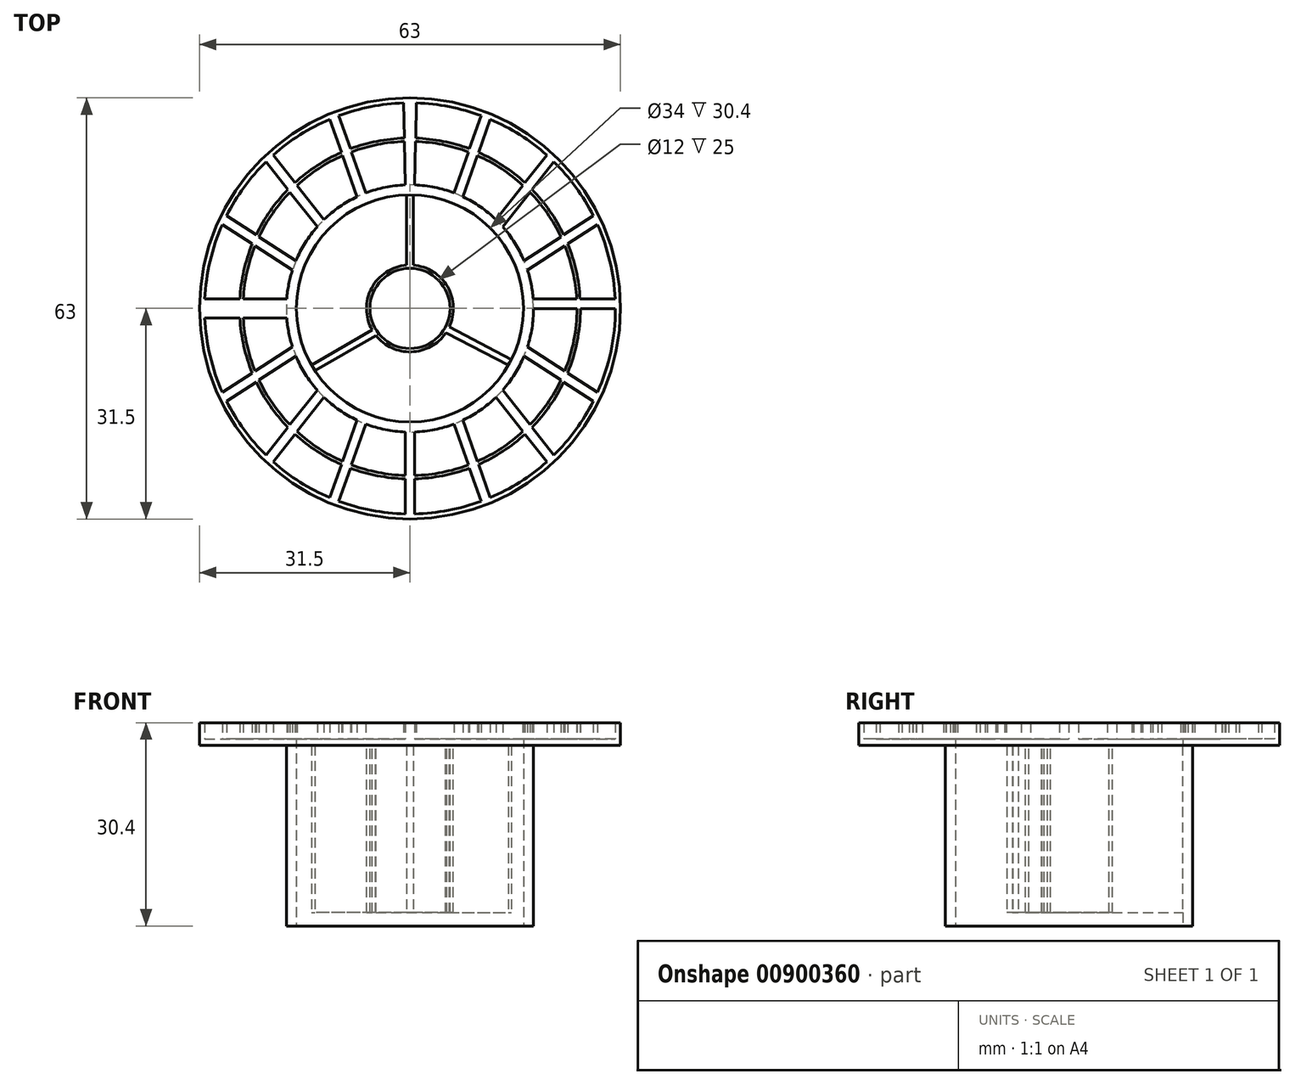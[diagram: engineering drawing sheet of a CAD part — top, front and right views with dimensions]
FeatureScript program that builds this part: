
annotation { "Feature Type Name" : "Feature", "Feature Type Description" : "" }
export const myFeature = defineFeature(function(context is Context, id is Id, definition is map)
    precondition{}
    {
        {
            var Q0;
            Q0=qCreatedBy(makeId("Top.planeOp"),FACE);
            var sketch = newSketch(context, id + "F0", { "sketchPlane" : qUnion([Q0])});
            skCircle(sketch, "E0", {"center": v(0, 0) * mm, "radius": 31.5 * mm});
            skArc(sketch, "E1", {"start": v(-0.7, 18.49) * mm, "mid": v(-3.7, 18.13) * mm, "end": v(-6.6, 17.29) * mm});
            skCircle(sketch, "E2", {"center": v(0, 0) * mm, "radius": 17 * mm});
            skArc(sketch, "E3", {"start": v(-0.85, 25.49) * mm, "mid": v(-4.94, 25.02) * mm, "end": v(-8.9, 23.9) * mm});
            skArc(sketch, "E4", {"start": v(-0.84, 24.99) * mm, "mid": v(-4.85, 24.52) * mm, "end": v(-8.74, 23.42) * mm});
            skArc(sketch, "E5", {"start": v(-0.96, 30.74) * mm, "mid": v(-5.88, 30.18) * mm, "end": v(-10.64, 28.85) * mm});
            skLineSegment(sketch, "E6.MirrorCS", {"start": v(0.96, 30.74) * mm, "end": v(0.85, 25.49) * mm});
            skPoint(sketch, "E7.start.orphan", {"position": v(0, 31.5) * mm});
            skLineSegment(sketch, "E8.trimOffspring", {"start": v(0.84, 24.99) * mm, "end": v(0.71, 18.49) * mm});
            skLineSegment(sketch, "E9", {"start": v(0.71, -18.49) * mm, "end": v(0.71, -24.99) * mm});
            skLineSegment(sketch, "E10", {"start": v(18.5, -0.03) * mm, "end": v(25, -0.03) * mm});
            skPoint(sketch, "E11.start.orphan", {"position": v(17, 0) * mm});
            skArc(sketch, "E12.trimOffspring", {"start": v(25.46, 1.42) * mm, "mid": v(24.87, 5.61) * mm, "end": v(23.6, 9.66) * mm});
            skArc(sketch, "E13.trimOffspring", {"start": v(24.96, 1.42) * mm, "mid": v(24.4, 5.47) * mm, "end": v(23.17, 9.38) * mm});
            skArc(sketch, "E14.trimOffspring", {"start": v(30.72, 1.42) * mm, "mid": v(29.92, 7.1) * mm, "end": v(28.07, 12.55) * mm});
            skLineSegment(sketch, "E15.trimOffspring", {"start": v(25.5, -0.03) * mm, "end": v(30.75, -0.03) * mm});
            skArc(sketch, "E16.trimOffspring", {"start": v(18.5, -0.14) * mm, "mid": v(18.5, -0.09) * mm, "end": v(18.5, -0.03) * mm});
            skPoint(sketch, "E17.orphan", {"position": v(0.71, -16.99) * mm});
            skPoint(sketch, "E18.orphan", {"position": v(-0.7, -16.99) * mm});
            skArc(sketch, "E19.trimOffspring", {"start": v(0.71, -24.99) * mm, "mid": v(4.8, -24.54) * mm, "end": v(8.74, -23.42) * mm});
            skArc(sketch, "E20.trimOffspring", {"start": v(0.71, -25.5) * mm, "mid": v(4.87, -25.03) * mm, "end": v(8.9, -23.9) * mm});
            skLineSegment(sketch, "E21.trimOffspring", {"start": v(0.71, -25.5) * mm, "end": v(0.71, -30.74) * mm});
            skArc(sketch, "E22.trimOffspring", {"start": v(0.71, -30.74) * mm, "mid": v(5.75, -30.2) * mm, "end": v(10.64, -28.85) * mm});
            skLineSegment(sketch, "E23", {"start": v(10.64, 28.85) * mm, "end": v(8.9, 23.9) * mm});
            skLineSegment(sketch, "E24", {"start": v(12, 28.32) * mm, "end": v(10.25, 23.35) * mm});
            skArc(sketch, "E25.trimOffspring", {"start": v(10.64, 28.85) * mm, "mid": v(5.88, 30.18) * mm, "end": v(0.96, 30.74) * mm});
            skPoint(sketch, "E26.orphan", {"position": v(10.89, 29.56) * mm});
            skLineSegment(sketch, "E27.trimOffspring", {"start": v(8.74, 23.42) * mm, "end": v(6.6, 17.29) * mm});
            skLineSegment(sketch, "E28.trimOffspring", {"start": v(10.08, 22.88) * mm, "end": v(7.93, 16.72) * mm});
            skArc(sketch, "E29.trimOffspring", {"start": v(6.6, 17.29) * mm, "mid": v(3.7, 18.13) * mm, "end": v(0.71, 18.49) * mm});
            skArc(sketch, "E30.trimOffspring", {"start": v(8.74, 23.42) * mm, "mid": v(4.85, 24.52) * mm, "end": v(0.84, 24.99) * mm});
            skArc(sketch, "E31.trimOffspring", {"start": v(8.9, 23.9) * mm, "mid": v(4.94, 25.02) * mm, "end": v(0.85, 25.49) * mm});
            skLineSegment(sketch, "E32", {"start": v(20.48, 22.93) * mm, "end": v(17.22, 18.8) * mm});
            skLineSegment(sketch, "E33", {"start": v(13.88, 12.24) * mm, "end": v(17.95, 17.4) * mm});
            skPoint(sketch, "E34.orphan", {"position": v(20.95, 23.52) * mm});
            skArc(sketch, "E35.trimOffspring", {"start": v(20.48, 22.93) * mm, "mid": v(16.46, 25.97) * mm, "end": v(12, 28.32) * mm});
            skPoint(sketch, "E36.orphan", {"position": v(22, 22.54) * mm});
            skLineSegment(sketch, "E37.trimOffspring", {"start": v(16.91, 18.41) * mm, "end": v(12.87, 13.3) * mm});
            skArc(sketch, "E38.trimOffspring", {"start": v(17.22, 18.8) * mm, "mid": v(13.92, 21.36) * mm, "end": v(10.25, 23.35) * mm});
            skArc(sketch, "E39.trimOffspring", {"start": v(16.91, 18.41) * mm, "mid": v(13.68, 20.92) * mm, "end": v(10.08, 22.88) * mm});
            skLineSegment(sketch, "E40.trimOffspring", {"start": v(18.27, 17.8) * mm, "end": v(21.54, 21.94) * mm});
            skArc(sketch, "E41.trimOffspring", {"start": v(12.87, 13.3) * mm, "mid": v(10.54, 15.2) * mm, "end": v(7.93, 16.72) * mm});
            skLineSegment(sketch, "E42", {"start": v(17.06, 7.15) * mm, "end": v(22.58, 10.72) * mm});
            skLineSegment(sketch, "E43", {"start": v(17.58, 5.76) * mm, "end": v(23.17, 9.38) * mm});
            skArc(sketch, "E44.trimOffspring", {"start": v(17.06, 7.15) * mm, "mid": v(15.68, 9.82) * mm, "end": v(13.88, 12.24) * mm});
            skArc(sketch, "E45.trimOffspring", {"start": v(27.44, 13.87) * mm, "mid": v(24.82, 18.15) * mm, "end": v(21.54, 21.94) * mm});
            skLineSegment(sketch, "E46", {"start": v(30.72, 1.42) * mm, "end": v(25.46, 1.42) * mm});
            skArc(sketch, "E47.trimOffspring", {"start": v(18.45, 1.42) * mm, "mid": v(18.14, 3.61) * mm, "end": v(17.58, 5.76) * mm});
            skLineSegment(sketch, "E48.trimOffspring", {"start": v(24.96, 1.42) * mm, "end": v(18.45, 1.42) * mm});
            skLineSegment(sketch, "E49.trimOffspring", {"start": v(23, 11) * mm, "end": v(27.44, 13.87) * mm});
            skArc(sketch, "E50.trimOffspring", {"start": v(23, 11) * mm, "mid": v(20.91, 14.6) * mm, "end": v(18.27, 17.8) * mm});
            skArc(sketch, "E51.trimOffspring", {"start": v(22.58, 10.72) * mm, "mid": v(20.54, 14.25) * mm, "end": v(17.95, 17.4) * mm});
            skLineSegment(sketch, "E52.trimOffspring", {"start": v(23.6, 9.66) * mm, "end": v(28.07, 12.55) * mm});
            skArc(sketch, "E53.MirrorCS", {"start": v(24.96, -1.42) * mm, "mid": v(24.4, -5.47) * mm, "end": v(23.17, -9.38) * mm});
            skArc(sketch, "E54.MirrorCS", {"start": v(23, -11) * mm, "mid": v(20.91, -14.6) * mm, "end": v(18.27, -17.8) * mm});
            skLineSegment(sketch, "E55.MirrorCS", {"start": v(13.88, -12.24) * mm, "end": v(17.95, -17.4) * mm});
            skLineSegment(sketch, "E56.MirrorCS", {"start": v(20.48, -22.93) * mm, "end": v(17.22, -18.8) * mm});
            skArc(sketch, "E57.MirrorCS", {"start": v(27.44, -13.87) * mm, "mid": v(24.82, -18.15) * mm, "end": v(21.54, -21.94) * mm});
            skLineSegment(sketch, "E58.MirrorCS", {"start": v(23.6, -9.66) * mm, "end": v(28.07, -12.55) * mm});
            skArc(sketch, "E59.MirrorCS", {"start": v(12.87, -13.3) * mm, "mid": v(10.54, -15.2) * mm, "end": v(7.93, -16.72) * mm});
            skArc(sketch, "E60.MirrorCS", {"start": v(16.91, -18.41) * mm, "mid": v(13.68, -20.92) * mm, "end": v(10.08, -22.88) * mm});
            skLineSegment(sketch, "E61.MirrorCS", {"start": v(16.91, -18.41) * mm, "end": v(12.87, -13.3) * mm});
            skArc(sketch, "E62.MirrorCS", {"start": v(8.9, -23.9) * mm, "mid": v(4.94, -25.02) * mm, "end": v(0.85, -25.49) * mm});
            skArc(sketch, "E63.MirrorCS", {"start": v(20.48, -22.93) * mm, "mid": v(16.46, -25.97) * mm, "end": v(12, -28.32) * mm});
            skLineSegment(sketch, "E64.MirrorCS", {"start": v(17.58, -5.76) * mm, "end": v(23.17, -9.38) * mm});
            skLineSegment(sketch, "E65.MirrorCS", {"start": v(23, -11) * mm, "end": v(27.44, -13.87) * mm});
            skLineSegment(sketch, "E66.MirrorCS", {"start": v(18.27, -17.8) * mm, "end": v(21.54, -21.94) * mm});
            skArc(sketch, "E67.MirrorCS", {"start": v(22.58, -10.72) * mm, "mid": v(20.54, -14.25) * mm, "end": v(17.95, -17.4) * mm});
            skLineSegment(sketch, "E68.MirrorCS", {"start": v(10.08, -22.88) * mm, "end": v(7.93, -16.72) * mm});
            skArc(sketch, "E69.MirrorCS", {"start": v(18.45, -1.42) * mm, "mid": v(18.14, -3.61) * mm, "end": v(17.58, -5.76) * mm});
            skPoint(sketch, "E70.MirrorP", {"position": v(20.95, -23.52) * mm});
            skArc(sketch, "E71.MirrorCS", {"start": v(17.06, -7.15) * mm, "mid": v(15.68, -9.82) * mm, "end": v(13.88, -12.24) * mm});
            skPoint(sketch, "E72.MirrorP", {"position": v(22, -22.54) * mm});
            skPoint(sketch, "E73.MirrorP", {"position": v(10.89, -29.56) * mm});
            skArc(sketch, "E74.MirrorCS", {"start": v(25.46, -1.42) * mm, "mid": v(24.87, -5.61) * mm, "end": v(23.6, -9.66) * mm});
            skArc(sketch, "E75.MirrorCS", {"start": v(10.64, -28.85) * mm, "mid": v(5.88, -30.18) * mm, "end": v(0.96, -30.74) * mm});
            skPoint(sketch, "E76.MirrorP", {"position": v(0, -31.5) * mm});
            skArc(sketch, "E77.MirrorCS", {"start": v(6.6, -17.29) * mm, "mid": v(3.7, -18.13) * mm, "end": v(0.71, -18.49) * mm});
            skLineSegment(sketch, "E78.MirrorCS", {"start": v(12, -28.32) * mm, "end": v(10.25, -23.35) * mm});
            skArc(sketch, "E79.MirrorCS", {"start": v(8.74, -23.42) * mm, "mid": v(4.85, -24.52) * mm, "end": v(0.84, -24.99) * mm});
            skLineSegment(sketch, "E80.MirrorCS", {"start": v(17.06, -7.15) * mm, "end": v(22.58, -10.72) * mm});
            skLineSegment(sketch, "E81.MirrorCS", {"start": v(8.74, -23.42) * mm, "end": v(6.6, -17.29) * mm});
            skLineSegment(sketch, "E82.MirrorCS", {"start": v(10.64, -28.85) * mm, "end": v(8.9, -23.9) * mm});
            skArc(sketch, "E83.MirrorCS", {"start": v(17.22, -18.8) * mm, "mid": v(13.92, -21.36) * mm, "end": v(10.25, -23.35) * mm});
            skArc(sketch, "E84.MirrorCS", {"start": v(30.72, -1.42) * mm, "mid": v(29.92, -7.1) * mm, "end": v(28.07, -12.55) * mm});
            skArc(sketch, "E85.MirrorCS", {"start": v(-24.96, -1.42) * mm, "mid": v(-24.4, -5.47) * mm, "end": v(-23.17, -9.38) * mm});
            skLineSegment(sketch, "E86.MirrorCS", {"start": v(-0.71, -25.5) * mm, "end": v(-0.71, -30.74) * mm});
            skArc(sketch, "E87.MirrorCS", {"start": v(-17.06, -7.15) * mm, "mid": v(-15.68, -9.82) * mm, "end": v(-13.88, -12.24) * mm});
            skLineSegment(sketch, "E88.MirrorCS", {"start": v(-0.71, -18.49) * mm, "end": v(-0.71, -24.99) * mm});
            skArc(sketch, "E89.MirrorCS", {"start": v(-22.58, -10.72) * mm, "mid": v(-20.54, -14.25) * mm, "end": v(-17.95, -17.4) * mm});
            skPoint(sketch, "E90.MirrorP", {"position": v(-10.89, -29.56) * mm});
            skLineSegment(sketch, "E91.MirrorCS", {"start": v(-13.88, 12.24) * mm, "end": v(-17.95, 17.4) * mm});
            skArc(sketch, "E92.MirrorCS", {"start": v(-22.58, 10.72) * mm, "mid": v(-20.54, 14.25) * mm, "end": v(-17.95, 17.4) * mm});
            skArc(sketch, "E93.MirrorCS", {"start": v(-18.45, -1.42) * mm, "mid": v(-18.14, -3.61) * mm, "end": v(-17.58, -5.76) * mm});
            skLineSegment(sketch, "E94.MirrorCS", {"start": v(-23, -11) * mm, "end": v(-27.44, -13.87) * mm});
            skArc(sketch, "E95.MirrorCS", {"start": v(-17.22, -18.8) * mm, "mid": v(-13.92, -21.36) * mm, "end": v(-10.25, -23.35) * mm});
            skPoint(sketch, "E96.MirrorP", {"position": v(0.7, -16.99) * mm});
            skLineSegment(sketch, "E97.MirrorCS", {"start": v(-0.84, 24.99) * mm, "end": v(-0.71, 18.49) * mm});
            skArc(sketch, "E98.MirrorCS", {"start": v(-0.71, -24.99) * mm, "mid": v(-4.8, -24.54) * mm, "end": v(-8.74, -23.42) * mm});
            skLineSegment(sketch, "E99.MirrorCS", {"start": v(-16.91, 18.41) * mm, "end": v(-12.87, 13.3) * mm});
            skArc(sketch, "E100.MirrorCS", {"start": v(-8.9, 23.9) * mm, "mid": v(-4.94, 25.02) * mm, "end": v(-0.85, 25.49) * mm});
            skLineSegment(sketch, "E101.MirrorCS", {"start": v(-23, 11) * mm, "end": v(-27.44, 13.87) * mm});
            skLineSegment(sketch, "E102.MirrorCS", {"start": v(-24.96, -1.42) * mm, "end": v(-18.45, -1.42) * mm});
            skLineSegment(sketch, "E103.MirrorCS", {"start": v(-17.58, -5.76) * mm, "end": v(-23.17, -9.38) * mm});
            skLineSegment(sketch, "E104.MirrorCS", {"start": v(-10.64, -28.85) * mm, "end": v(-8.9, -23.9) * mm});
            skPoint(sketch, "E105.MirrorP", {"position": v(-22, 22.54) * mm});
            skArc(sketch, "E106.MirrorCS", {"start": v(-16.91, 18.41) * mm, "mid": v(-13.68, 20.92) * mm, "end": v(-10.08, 22.88) * mm});
            skArc(sketch, "E107.MirrorCS", {"start": v(-8.74, 23.42) * mm, "mid": v(-4.85, 24.52) * mm, "end": v(-0.84, 24.99) * mm});
            skLineSegment(sketch, "E108.MirrorCS", {"start": v(-13.88, -12.24) * mm, "end": v(-17.95, -17.4) * mm});
            skLineSegment(sketch, "E109.MirrorCS", {"start": v(-30.72, 1.42) * mm, "end": v(-25.46, 1.42) * mm});
            skArc(sketch, "E110.MirrorCS", {"start": v(-23, -11) * mm, "mid": v(-20.91, -14.6) * mm, "end": v(-18.27, -17.8) * mm});
            skArc(sketch, "E111.MirrorCS", {"start": v(-18.45, 1.42) * mm, "mid": v(-18.14, 3.61) * mm, "end": v(-17.58, 5.76) * mm});
            skArc(sketch, "E112.MirrorCS", {"start": v(-0.71, -18.49) * mm, "mid": v(-3.7, -18.13) * mm, "end": v(-6.6, -17.29) * mm});
            skArc(sketch, "E113.MirrorCS", {"start": v(-30.72, 1.42) * mm, "mid": v(-29.92, 7.1) * mm, "end": v(-28.07, 12.55) * mm});
            skLineSegment(sketch, "E114.MirrorCS", {"start": v(-8.74, 23.42) * mm, "end": v(-6.6, 17.29) * mm});
            skLineSegment(sketch, "E115.MirrorCS", {"start": v(-0.96, 30.74) * mm, "end": v(-0.85, 25.49) * mm});
            skArc(sketch, "E116.MirrorCS", {"start": v(-25.46, 1.42) * mm, "mid": v(-24.87, 5.61) * mm, "end": v(-23.6, 9.66) * mm});
            skPoint(sketch, "E117.MirrorP", {"position": v(-20.95, 23.52) * mm});
            skArc(sketch, "E118.MirrorCS", {"start": v(-27.44, -13.87) * mm, "mid": v(-24.82, -18.15) * mm, "end": v(-21.54, -21.94) * mm});
            skLineSegment(sketch, "E119.MirrorCS", {"start": v(-20.48, 22.93) * mm, "end": v(-17.22, 18.8) * mm});
            skPoint(sketch, "E120.MirrorP", {"position": v(-17, 0) * mm});
            skLineSegment(sketch, "E121.MirrorCS", {"start": v(-12, -28.32) * mm, "end": v(-10.25, -23.35) * mm});
            skArc(sketch, "E122.MirrorCS", {"start": v(-23, 11) * mm, "mid": v(-20.91, 14.6) * mm, "end": v(-18.27, 17.8) * mm});
            skArc(sketch, "E123.MirrorCS", {"start": v(-6.6, -17.29) * mm, "mid": v(-3.7, -18.13) * mm, "end": v(-0.71, -18.49) * mm});
            skLineSegment(sketch, "E124.MirrorCS", {"start": v(-16.91, -18.41) * mm, "end": v(-12.87, -13.3) * mm});
            skLineSegment(sketch, "E125.MirrorCS", {"start": v(-17.06, -7.15) * mm, "end": v(-22.58, -10.72) * mm});
            skArc(sketch, "E126.MirrorCS", {"start": v(-12.87, -13.3) * mm, "mid": v(-10.54, -15.2) * mm, "end": v(-7.93, -16.72) * mm});
            skLineSegment(sketch, "E127.MirrorCS", {"start": v(-24.96, 1.42) * mm, "end": v(-18.45, 1.42) * mm});
            skLineSegment(sketch, "E128.MirrorCS", {"start": v(-18.27, -17.8) * mm, "end": v(-21.54, -21.94) * mm});
            skLineSegment(sketch, "E129.MirrorCS", {"start": v(-30.72, -1.42) * mm, "end": v(-25.46, -1.42) * mm});
            skArc(sketch, "E130.MirrorCS", {"start": v(-24.96, 1.42) * mm, "mid": v(-24.4, 5.47) * mm, "end": v(-23.17, 9.38) * mm});
            skArc(sketch, "E131.MirrorCS", {"start": v(-17.06, 7.15) * mm, "mid": v(-15.68, 9.82) * mm, "end": v(-13.88, 12.24) * mm});
            skLineSegment(sketch, "E132.MirrorCS", {"start": v(-8.74, -23.42) * mm, "end": v(-6.6, -17.29) * mm});
            skArc(sketch, "E133.MirrorCS", {"start": v(-0.71, -25.5) * mm, "mid": v(-4.87, -25.03) * mm, "end": v(-8.9, -23.9) * mm});
            skArc(sketch, "E134.MirrorCS", {"start": v(-8.74, -23.42) * mm, "mid": v(-4.85, -24.52) * mm, "end": v(-0.84, -24.99) * mm});
            skArc(sketch, "E135.MirrorCS", {"start": v(-30.72, -1.42) * mm, "mid": v(-29.92, -7.1) * mm, "end": v(-28.07, -12.55) * mm});
            skArc(sketch, "E136.MirrorCS", {"start": v(-0.71, -30.74) * mm, "mid": v(-5.75, -30.2) * mm, "end": v(-10.64, -28.85) * mm});
            skLineSegment(sketch, "E137.MirrorCS", {"start": v(-10.08, -22.88) * mm, "end": v(-7.93, -16.72) * mm});
            skArc(sketch, "E138.MirrorCS", {"start": v(-12.87, 13.3) * mm, "mid": v(-10.54, 15.2) * mm, "end": v(-7.93, 16.72) * mm});
            skPoint(sketch, "E139.MirrorP", {"position": v(-20.95, -23.52) * mm});
            skLineSegment(sketch, "E140.MirrorCS", {"start": v(-17.06, 7.15) * mm, "end": v(-22.58, 10.72) * mm});
            skArc(sketch, "E141.MirrorCS", {"start": v(-20.48, -22.93) * mm, "mid": v(-16.46, -25.97) * mm, "end": v(-12, -28.32) * mm});
            skArc(sketch, "E142.MirrorCS", {"start": v(-16.91, -18.41) * mm, "mid": v(-13.68, -20.92) * mm, "end": v(-10.08, -22.88) * mm});
            skArc(sketch, "E143.MirrorCS", {"start": v(-17.22, 18.8) * mm, "mid": v(-13.92, 21.36) * mm, "end": v(-10.25, 23.35) * mm});
            skArc(sketch, "E144.MirrorCS", {"start": v(-20.48, 22.93) * mm, "mid": v(-16.46, 25.97) * mm, "end": v(-12, 28.32) * mm});
            skArc(sketch, "E145.MirrorCS", {"start": v(-8.9, -23.9) * mm, "mid": v(-4.94, -25.02) * mm, "end": v(-0.85, -25.49) * mm});
            skLineSegment(sketch, "E146.MirrorCS", {"start": v(-23.6, 9.66) * mm, "end": v(-28.07, 12.55) * mm});
            skArc(sketch, "E147.MirrorCS", {"start": v(-10.64, 28.85) * mm, "mid": v(-5.88, 30.18) * mm, "end": v(-0.96, 30.74) * mm});
            skArc(sketch, "E148.MirrorCS", {"start": v(-27.44, 13.87) * mm, "mid": v(-24.82, 18.15) * mm, "end": v(-21.54, 21.94) * mm});
            skPoint(sketch, "E149.MirrorP", {"position": v(-0.71, -16.99) * mm});
            skArc(sketch, "E150.MirrorCS", {"start": v(-25.46, -1.42) * mm, "mid": v(-24.87, -5.61) * mm, "end": v(-23.6, -9.66) * mm});
            skLineSegment(sketch, "E151.MirrorCS", {"start": v(-10.64, 28.85) * mm, "end": v(-8.9, 23.9) * mm});
            skLineSegment(sketch, "E152.MirrorCS", {"start": v(-20.48, -22.93) * mm, "end": v(-17.22, -18.8) * mm});
            skLineSegment(sketch, "E153.MirrorCS", {"start": v(-18.27, 17.8) * mm, "end": v(-21.54, 21.94) * mm});
            skArc(sketch, "E154.MirrorCS", {"start": v(-6.6, 17.29) * mm, "mid": v(-3.7, 18.13) * mm, "end": v(-0.71, 18.49) * mm});
            skLineSegment(sketch, "E155.MirrorCS", {"start": v(-17.58, 5.76) * mm, "end": v(-23.17, 9.38) * mm});
            skPoint(sketch, "E156.MirrorP", {"position": v(-10.89, 29.56) * mm});
            skLineSegment(sketch, "E157.MirrorCS", {"start": v(-23.6, -9.66) * mm, "end": v(-28.07, -12.55) * mm});
            skLineSegment(sketch, "E158.MirrorCS", {"start": v(-10.08, 22.88) * mm, "end": v(-7.93, 16.72) * mm});
            skArc(sketch, "E159.MirrorCS", {"start": v(-10.64, -28.85) * mm, "mid": v(-5.88, -30.18) * mm, "end": v(-0.96, -30.74) * mm});
            skPoint(sketch, "E160.MirrorP", {"position": v(-22, -22.54) * mm});
            skLineSegment(sketch, "E161.MirrorCS", {"start": v(-12, 28.32) * mm, "end": v(-10.25, 23.35) * mm});
            skArc(sketch, "E162.trimOffspring", {"start": v(-10.25, 23.35) * mm, "mid": v(-13.92, 21.36) * mm, "end": v(-17.22, 18.8) * mm});
            skArc(sketch, "E163.trimOffspring", {"start": v(-10.08, 22.88) * mm, "mid": v(-13.68, 20.92) * mm, "end": v(-16.91, 18.41) * mm});
            skArc(sketch, "E164.trimOffspring", {"start": v(-7.93, 16.72) * mm, "mid": v(-10.54, 15.2) * mm, "end": v(-12.87, 13.3) * mm});
            skArc(sketch, "E165.trimOffspring", {"start": v(-21.54, 21.94) * mm, "mid": v(-24.82, 18.15) * mm, "end": v(-27.44, 13.87) * mm});
            skArc(sketch, "E166.trimOffspring", {"start": v(-18.27, 17.8) * mm, "mid": v(-20.91, 14.6) * mm, "end": v(-23, 11) * mm});
            skArc(sketch, "E167.trimOffspring", {"start": v(-17.95, 17.4) * mm, "mid": v(-20.54, 14.25) * mm, "end": v(-22.58, 10.72) * mm});
            skArc(sketch, "E168.trimOffspring", {"start": v(-13.88, 12.24) * mm, "mid": v(-15.68, 9.82) * mm, "end": v(-17.06, 7.15) * mm});
            skArc(sketch, "E169.trimOffspring", {"start": v(-28.07, 12.55) * mm, "mid": v(-29.92, 7.1) * mm, "end": v(-30.72, 1.42) * mm});
            skPoint(sketch, "E170.orphan", {"position": v(-30.75, -0.03) * mm});
            skPoint(sketch, "E171.orphan", {"position": v(-25.5, -0.03) * mm});
            skPoint(sketch, "E172.orphan", {"position": v(-25, -0.03) * mm});
            skPoint(sketch, "E173.MirrorCS.end.orphan", {"position": v(-18.5, -0.03) * mm});
            skPoint(sketch, "E173.MirrorCS.start.orphan", {"position": v(-18.5, -0.14) * mm});
            skArc(sketch, "E174.trimOffspring", {"start": v(-23.6, -9.66) * mm, "mid": v(-24.87, -5.61) * mm, "end": v(-25.46, -1.42) * mm});
            skArc(sketch, "E175.trimOffspring", {"start": v(-28.07, -12.55) * mm, "mid": v(-29.92, -7.1) * mm, "end": v(-30.72, -1.42) * mm});
            skArc(sketch, "E176.trimOffspring", {"start": v(-23.17, -9.38) * mm, "mid": v(-24.4, -5.47) * mm, "end": v(-24.96, -1.42) * mm});
            skArc(sketch, "E177.trimOffspring", {"start": v(-17.58, -5.76) * mm, "mid": v(-18.14, -3.61) * mm, "end": v(-18.45, -1.42) * mm});
            skArc(sketch, "E178.trimOffspring", {"start": v(-17.95, -17.4) * mm, "mid": v(-20.54, -14.25) * mm, "end": v(-22.58, -10.72) * mm});
            skArc(sketch, "E179.trimOffspring", {"start": v(-18.27, -17.8) * mm, "mid": v(-20.91, -14.6) * mm, "end": v(-23, -11) * mm});
            skArc(sketch, "E180.trimOffspring", {"start": v(-13.88, -12.24) * mm, "mid": v(-15.68, -9.82) * mm, "end": v(-17.06, -7.15) * mm});
            skArc(sketch, "E181.trimOffspring", {"start": v(-21.54, -21.94) * mm, "mid": v(-24.82, -18.15) * mm, "end": v(-27.44, -13.87) * mm});
            skArc(sketch, "E182.trimOffspring", {"start": v(-7.93, -16.72) * mm, "mid": v(-10.54, -15.2) * mm, "end": v(-12.87, -13.3) * mm});
            skArc(sketch, "E183.trimOffspring", {"start": v(-10.08, -22.88) * mm, "mid": v(-13.68, -20.92) * mm, "end": v(-16.91, -18.41) * mm});
            skArc(sketch, "E184.trimOffspring", {"start": v(-8.9, -23.9) * mm, "mid": v(-4.87, -25.03) * mm, "end": v(-0.7, -25.5) * mm});
            skArc(sketch, "E185.trimOffspring", {"start": v(-12, -28.32) * mm, "mid": v(-16.46, -25.97) * mm, "end": v(-20.48, -22.93) * mm});
            skArc(sketch, "E186.trimOffspring", {"start": v(-6.6, -17.29) * mm, "mid": v(-3.7, -18.13) * mm, "end": v(-0.7, -18.49) * mm});
            skArc(sketch, "E187.trimOffspring", {"start": v(-8.74, -23.42) * mm, "mid": v(-4.8, -24.54) * mm, "end": v(-0.71, -24.99) * mm});
            skArc(sketch, "E188.trimOffspring", {"start": v(-10.25, -23.35) * mm, "mid": v(-13.92, -21.36) * mm, "end": v(-17.22, -18.8) * mm});
            skArc(sketch, "E189.trimOffspring", {"start": v(-10.64, -28.85) * mm, "mid": v(-5.75, -30.2) * mm, "end": v(-0.7, -30.74) * mm});
            skArc(sketch, "E190.trimOffspring", {"start": v(12, -28.32) * mm, "mid": v(16.46, -25.97) * mm, "end": v(20.48, -22.93) * mm});
            skArc(sketch, "E191.trimOffspring", {"start": v(10.08, -22.88) * mm, "mid": v(13.68, -20.92) * mm, "end": v(16.91, -18.41) * mm});
            skArc(sketch, "E192.trimOffspring", {"start": v(10.25, -23.35) * mm, "mid": v(13.92, -21.36) * mm, "end": v(17.22, -18.8) * mm});
            skArc(sketch, "E193.trimOffspring", {"start": v(7.93, -16.72) * mm, "mid": v(10.54, -15.2) * mm, "end": v(12.87, -13.3) * mm});
            skArc(sketch, "E194.trimOffspring", {"start": v(13.88, -12.24) * mm, "mid": v(15.68, -9.82) * mm, "end": v(17.06, -7.15) * mm});
            skArc(sketch, "E195.trimOffspring", {"start": v(17.95, -17.4) * mm, "mid": v(20.54, -14.25) * mm, "end": v(22.58, -10.72) * mm});
            skArc(sketch, "E196.trimOffspring", {"start": v(18.27, -17.8) * mm, "mid": v(20.91, -14.6) * mm, "end": v(23, -11) * mm});
            skArc(sketch, "E197.trimOffspring", {"start": v(21.54, -21.94) * mm, "mid": v(24.82, -18.15) * mm, "end": v(27.44, -13.87) * mm});
            skArc(sketch, "E198.trimOffspring", {"start": v(17.58, -5.76) * mm, "mid": v(18.27, -2.93) * mm, "end": v(18.5, -0.03) * mm});
            skArc(sketch, "E199.trimOffspring", {"start": v(23.17, -9.38) * mm, "mid": v(24.54, -4.8) * mm, "end": v(25, -0.03) * mm});
            skArc(sketch, "E200.trimOffspring", {"start": v(23.6, -9.66) * mm, "mid": v(25.02, -4.94) * mm, "end": v(25.5, -0.03) * mm});
            skArc(sketch, "E201.trimOffspring", {"start": v(28.07, -12.55) * mm, "mid": v(30.07, -6.43) * mm, "end": v(30.75, -0.03) * mm});
            skSolve(sketch);
        }
        {
            var Q0;
            Q0=makeQuery(id+"F0.imprint","IMPRINT",FACE,{"disambiguationData":[TD([[makeQuery(id+"F0.imprint","IMPRINT",EDGE,{"derivedFrom":sQuery(id+"F0.wireOp",EDGE,"E0")}),1.0]])]});
            extrude(context, id + "F1", {"entities" : qUnion([Q0]), "depth" : 3.4 * mm, "offsetDistance" : 25 * mm});
        }
        {
            var Q0;
            Q0=qCreatedBy(makeId("Top.planeOp"),FACE);
            var sketch = newSketch(context, id + "F2", { "sketchPlane" : qUnion([Q0])});
            skCircle(sketch, "E202", {"center": v(0, 0) * mm, "radius": 31.5 * mm});
            skCircle(sketch, "E203", {"center": v(0, 0) * mm, "radius": 18.5 * mm});
            skCircle(sketch, "E204", {"center": v(0, 0) * mm, "radius": 17 * mm});
            skSolve(sketch);
        }
        {
            var Q0;
            Q0 = qSketchRegion(id + "F2", true);
            extrude(context, id + "F3", {"entities" : qUnion([Q0]), "operationType" : NewBodyOperationType.ADD, "depth" : 1 * mm, "offsetDistance" : 25 * mm});
        }
        {
            var Q0;
            Q0=qCreatedBy(makeId("Top.planeOp"),FACE);
            var sketch = newSketch(context, id + "F4", { "sketchPlane" : qUnion([Q0])});
            skCircle(sketch, "E205", {"center": v(0, 0) * mm, "radius": 18.5 * mm});
            skCircle(sketch, "E206", {"center": v(0, 0) * mm, "radius": 17 * mm});
            skSolve(sketch);
        }
        {
            var Q0;
            Q0 = qSketchRegion(id + "F4", true);
            extrude(context, id + "F5", {"entities" : qUnion([Q0]), "operationType" : NewBodyOperationType.ADD, "oppositeDirection" : true, "depth" : 27 * mm, "offsetDistance" : 25 * mm});
        }
        {
            var Q0;
            Q0=qCreatedBy(makeId("Top.planeOp"),FACE);
            var sketch = newSketch(context, id + "F6", { "sketchPlane" : qUnion([Q0])});
            skArc(sketch, "E207", {"start": v(-0.5, 6.48) * mm, "mid": v(-5.74, 3.04) * mm, "end": v(-5.64, -3.23) * mm});
            skCircle(sketch, "E208", {"center": v(0, 0) * mm, "radius": 6 * mm});
            skLineSegment(sketch, "E209", {"start": v(-0.5, 6.48) * mm, "end": v(-0.5, 17.1) * mm});
            skLineSegment(sketch, "E210.MirrorCS", {"start": v(0.5, 6.48) * mm, "end": v(0.5, 17.1) * mm});
            skPoint(sketch, "E211.end.orphan", {"position": v(0, 17.1) * mm});
            skPoint(sketch, "E211.start.orphan", {"position": v(0, 6.5) * mm});
            skLineSegment(sketch, "E212", {"start": v(-0.5, 17.1) * mm, "end": v(0.5, 17.1) * mm});
            skLineSegment(sketch, "E213", {"start": v(5.88, -2.77) * mm, "end": v(15.48, -7.77) * mm});
            skLineSegment(sketch, "E214.MirrorCS", {"start": v(5.52, -3.72) * mm, "end": v(15.01, -8.66) * mm});
            skLineSegment(sketch, "E215", {"start": v(5.33, -3.72) * mm, "end": v(5.52, -3.72) * mm});
            skArc(sketch, "E216.trimOffspring", {"start": v(5.88, -2.77) * mm, "mid": v(5.62, 3.27) * mm, "end": v(0.5, 6.48) * mm});
            skLineSegment(sketch, "E217", {"start": v(15.48, -7.77) * mm, "end": v(15.01, -8.66) * mm});
            skLineSegment(sketch, "E218", {"start": v(-5.64, -3.23) * mm, "end": v(-14.78, -8.46) * mm});
            skLineSegment(sketch, "E219.MirrorCS", {"start": v(-5.14, -4.1) * mm, "end": v(-14.29, -9.33) * mm});
            skLineSegment(sketch, "E220", {"start": v(-14.78, -8.46) * mm, "end": v(-14.29, -9.33) * mm});
            skLineSegment(sketch, "E221", {"start": v(-5.08, -4.05) * mm, "end": v(-5.14, -4.1) * mm});
            skArc(sketch, "E222.trimOffspring", {"start": v(-5.08, -4.05) * mm, "mid": v(0.2, -6.5) * mm, "end": v(5.33, -3.72) * mm});
            skLineSegment(sketch, "E223", {"start": v(-5.08, -4.05) * mm, "end": v(-5.06, -4.05) * mm});
            skSolve(sketch);
        }
        {
            var Q0;
            Q0=makeQuery(id+"F6.imprint","IMPRINT",FACE,{"disambiguationData":[TD([[makeQuery(id+"F6.imprint","IMPRINT",EDGE,{"derivedFrom":sQuery(id+"F6.wireOp",EDGE,"E207")}),1.0]])]});
            extrude(context, id + "F7", {"entities" : qUnion([Q0]), "operationType" : NewBodyOperationType.ADD, "oppositeDirection" : true, "depth" : 25 * mm, "offsetDistance" : 25 * mm});
        }
    });
